# Revit family: IS_ConceptAir_E0822_BIM_GB
name_source: partatom
category: Plumbing Fixtures
revit_build: Autodesk Revit MEP 2014 (Build: 20140709_2115(x64)
units: mm (PartAtom-declared; Revit-internal decimal feet)

## types (6) — shared parameters
Accessories = www.idealspec.co.uk
AreaUnits = millimeters
Assembly Code = C1030200
AssetType = Fixed
BREEAM = No
Brand = IdealStandard
Default Elevation = 800 mm
DurationUnit = year
ECA = No
ExpectedLife = 30
IfcExportAs = IfcFurnitureType
IfcExportType = USERDEFINED
InstallationInstructions = www.idealspec.co.uk/resources.html
LinearUnits = millimeters
ManufacturerURL = www.idealspec.co.uk
Material = Laquered MDF
NBSDescription = Bathroom integrated duct work
NBSReference = 45-35-72/320
NettWeight = 0 Kg
NominalDepth = 440 mm  [stored 1.44357 ft]
NominalHeight = 517 mm  [stored 1.69619 ft]
NominalLength = 440 mm  [stored 1.44357 ft]
NominalWidth = 1200 mm
Shape = Rectangular
Size = 517 x 440 x 1200 mm
Space = Internal
SpareParts = www.fastpart-spares.co.uk
TMV3 = No
URL = www.idealspec.co.uk
Uniclass2 = Pr_40_30_78_04
Version = 1
VolumeUnits = Litres
WRAS = No
WarrantyDescription = Manufacturers warranty
WarrantyDurationParts = 5
WarrantyDurationUnit = year
WaterEfficientProduct = No
zero-valued in all types: CWFU, Cost, HWFU, WFU

## per-type parameters (varying)
| type | BIMObjectName | Color | Description | Features | Finish | InnerColour | MainColor | MainColour | Model | ModelNumber | ModelReference | Name | ProductInformation |
| E0822UK - 120CM Wall Hung Vanity Unit 4 Drawer Wood Light Brown + Matt Light Brown | ISI_IdealStandard_Furniture_ConceptAir_E0822UK | Wood brown | Concept Air 120 cm Wall Hung Vanity Unit 4 Drawer Wood Light Brown + Matt Light Brown | 120 cm Wall Hung Vanity Unit 4 Drawer Wood Light Brown + Matt Light Brown | Wood brown | ISI_IdealStandard_Furniture_WoodLightBrown_Render | Wood brown | ISI_IdealStandard_Furniture_WoodLightBrown_Render | E0822UK | E0822UK | Concept Air 120 cm Wall Hung Vanity Unit 4 Drawer Wood Light Brown + Matt Light Brown | Furniture_ConceptAir_E0822UK_IdealStandard | www.idealspec.co.uk/assets/datasheet/E0822UK |
| E0822PS - 120CM Wall Hung Vanity Unit 4 Drawer Wood Light Grey + Matt White | ISI_IdealStandard_Furniture_ConceptAir_E0822PS | Wood grey | Concept Air 120 cm Wall Hung Vanity Unit 4 Drawer Wood Light Grey + Matt White | 120 cm Wall Hung Vanity Unit 4 Drawer Wood Light Grey + Matt White | Wood grey | ISI_IdealStandard_Laminate_White_Render | Wood grey | ISI_IdealStandard_Furniture_WoodLightGrey_Render | E0822PS | E0822PS | Concept Air 120 cm Wall Hung Vanity Unit 4 Drawer Wood Light Grey + Matt White | Furniture_ConceptAir_E0822PS_IdealStandard | www.idealspec.co.uk/assets/datasheet/E0822PS |
| E0822KN - 120CM Wall Hung Vanity Unit 4 Drawer Gls White + Matt Light Grey | ISI_IdealStandard_Furniture_ConceptAir_E0822KN | White | Concept Air 120 cm Wall Hung Vanity Unit 4 Drawer Gls White + Matt Light Grey | 120 cm Wall Hung Vanity Unit 4 Drawer Gls White + Matt Light Grey | White | ISI_IdealStandard_Furniture_Grey_Render | White | ISI_IdealStandard_Laminate_White_Render | E0822KN | E0822KN | Concept Air 120 cm Wall Hung Vanity Unit 4 Drawer Gls White + Matt Light Grey | Furniture_ConceptAir_E0822KN_IdealStandard | www.idealspec.co.uk/assets/datasheet/E0822KN |
| E0822EQ - 120CM Wall Hung Vanity Unit 4 Drawer Gls Light Grey + Matt White | ISI_IdealStandard_Furniture_ConceptAir_E0822EQ | Grey | Concept Air 120 cm Wall Hung Vanity Unit 4 Drawer Gls Light Grey + Matt White | 120 cm Wall Hung Vanity Unit 4 Drawer Gls Light Grey + Matt White | Grey | ISI_IdealStandard_Laminate_White_Render | Grey | ISI_IdealStandard_Furniture_Grey_Render | E0822EQ | E0822EQ | Concept Air 120 cm Wall Hung Vanity Unit 4 Drawer Gls Light Grey + Matt White | Furniture_ConceptAir_E0822EQ_IdealStandard | www.idealspec.co.uk/assets/datasheet/E0822EQ |
| E0822B2 - 120CM Wall Hung Vanity Unit 4 Drawer Gls White + Matt White | ISI_IdealStandard_Furniture_ConceptAir_E0822B2 | White | Concept Air 120 cm Wall Hung Vanity Unit 4 Drawer Gls White + Matt White | 120 cm Wall Hung Vanity Unit 4 Drawer Gls White + Matt White | White | ISI_IdealStandard_Laminate_White_Render | White | ISI_IdealStandard_Laminate_White_Render | E0822B2 | E0822B2 | Concept Air 120 cm Wall Hung Vanity Unit 4 Drawer Gls White + Matt White | Furniture_ConceptAir_E0822B2_IdealStandard | www.idealspec.co.uk/assets/datasheet/E0822B2 |
| E0822VY - 120CM Wall Hung Vanity Unit 4 Drawer Matt Dark Brown + Matt White | ISI_IdealStandard_Furniture_ConceptAir_E0822VY | Dark brown | Concept Air 120 cm Wall Hung Vanity Unit 4 Drawer Matt Dark Brown + Matt White | 120 cm Wall Hung Vanity Unit 4 Drawer Matt Dark Brown + Matt White | Dark brown | ISI_IdealStandard_Laminate_White_Render | Dark brown | ISI_IdealStandard_Furniture_DarkBrown_Render | E0822VY | E0822VY | Concept Air 120 cm Wall Hung Vanity Unit 4 Drawer Gls Dark Brown + Matt White | Furniture_ConceptAir_E0822VY_IdealStandard | www.idealspec.co.uk/assets/datasheet/E0822VY |

note: [stored X ft] marks values corroborated as IEEE doubles in the binary element streams (Revit-internal decimal feet)

## geometry (parser evidence)
native form markers: Sweep x1
no freeform markers — native parametric forms only
